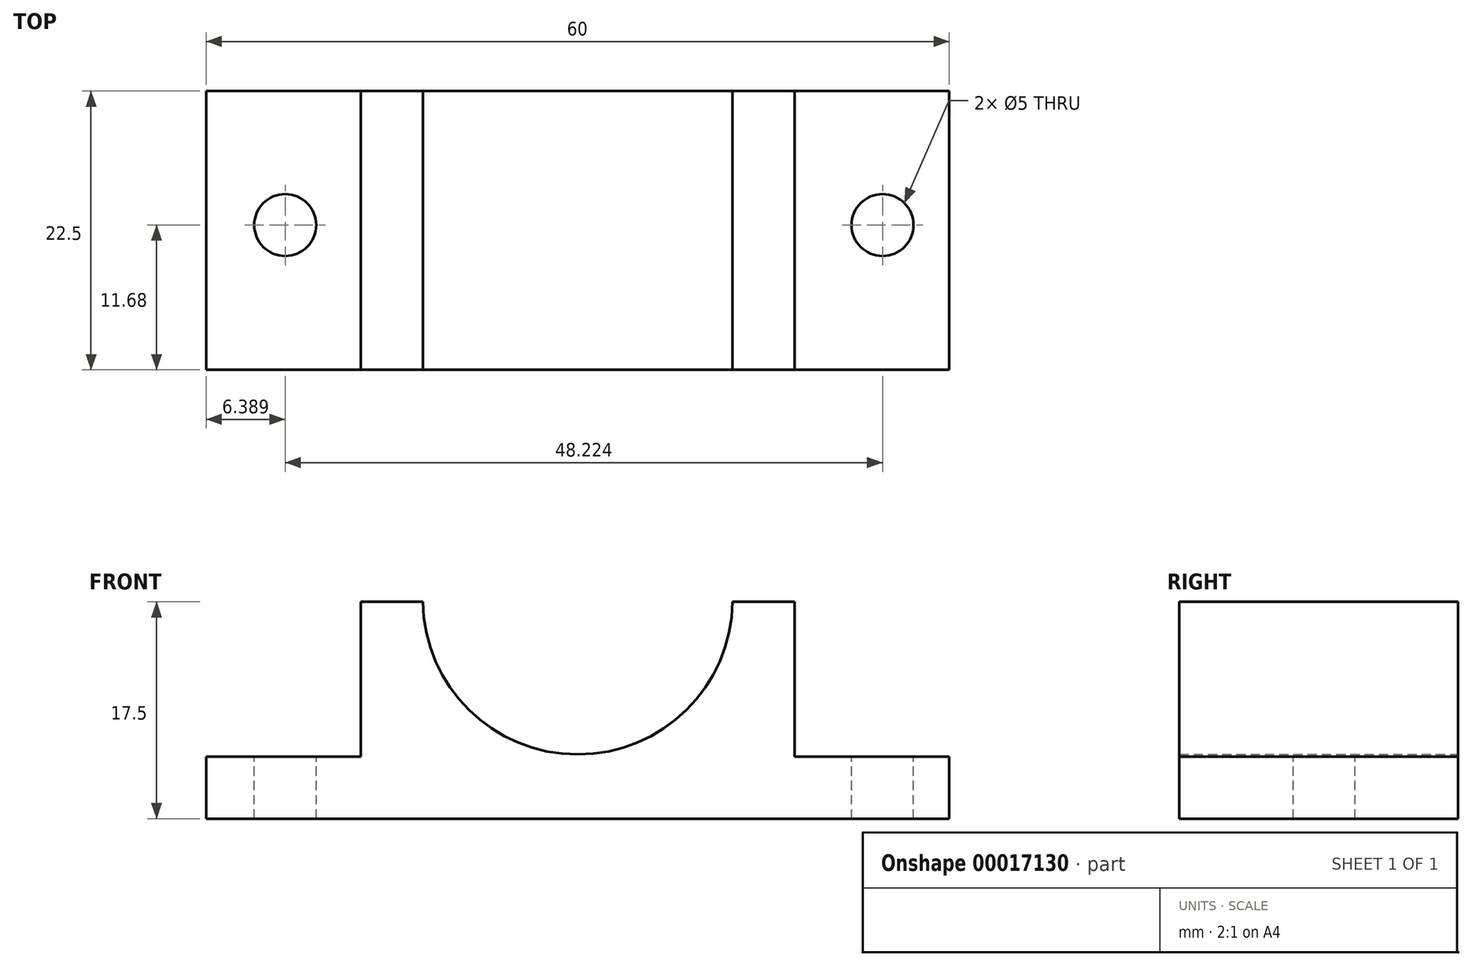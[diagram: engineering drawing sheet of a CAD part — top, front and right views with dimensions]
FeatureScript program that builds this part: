
annotation { "Feature Type Name" : "Feature", "Feature Type Description" : "" }
export const myFeature = defineFeature(function(context is Context, id is Id, definition is map)
    precondition{}
    {
        {
            var Q0;
            Q0=qCreatedBy(makeId("Front.planeOp"),FACE);
            var sketch = newSketch(context, id + "F0", { "sketchPlane" : qUnion([Q0])});
            skLineSegment(sketch, "E0.top", {"start": v(-15.67, -12.96) * mm, "end": v(44.33, -12.96) * mm});
            skLineSegment(sketch, "E0.left", {"start": v(-15.67, -7.96) * mm, "end": v(-15.67, -12.96) * mm});
            skLineSegment(sketch, "E0.right", {"start": v(44.33, -7.96) * mm, "end": v(44.33, -12.96) * mm});
            skLineSegment(sketch, "E1.left", {"start": v(-3.17, -7.96) * mm, "end": v(-3.17, 4.54) * mm});
            skLineSegment(sketch, "E1.right", {"start": v(31.83, -7.96) * mm, "end": v(31.83, 4.54) * mm});
            skArc(sketch, "E2", {"start": v(1.83, 4.54) * mm, "mid": v(14.33, -7.78) * mm, "end": v(26.83, 4.54) * mm});
            skLineSegment(sketch, "E3", {"start": v(-15.67, -7.96) * mm, "end": v(-3.17, -7.96) * mm});
            skLineSegment(sketch, "E4", {"start": v(31.83, -7.96) * mm, "end": v(44.33, -7.96) * mm});
            skLineSegment(sketch, "E5", {"start": v(-3.17, 4.54) * mm, "end": v(1.83, 4.54) * mm});
            skLineSegment(sketch, "E6", {"start": v(26.83, 4.54) * mm, "end": v(31.83, 4.54) * mm});
            skSolve(sketch);
        }
        {
            var Q0;
            Q0=makeQuery(id+"F0.imprint","IMPRINT",FACE,{"disambiguationData":[TD([[makeQuery(id+"F0.imprint","IMPRINT",EDGE,{"derivedFrom":sQuery(id+"F0.wireOp",EDGE,"E0.top")}),1.0]])]});
            extrude(context, id + "F1", {"entities" : qUnion([Q0]), "depth" : 22.5 * mm});
        }
        {
            var Q0;
            Q0=qCreatedBy(makeId("Top.planeOp"),FACE);
            var sketch = newSketch(context, id + "F2", { "sketchPlane" : qUnion([Q0])});
            skCircle(sketch, "E7", {"center": v(-9.28, -10.82) * mm, "radius": 2.5 * mm});
            skCircle(sketch, "E8", {"center": v(38.94, -10.82) * mm, "radius": 2.5 * mm});
            skSolve(sketch);
        }
        {
            var Q0;
            Q0=makeQuery(id+"F2.imprint","IMPRINT",FACE,{"disambiguationData":[TD([[makeQuery(id+"F2.imprint","IMPRINT",EDGE,{"derivedFrom":sQuery(id+"F2.wireOp",EDGE,"E7")}),1.0]])]});
            var Q1;
            Q1=makeQuery(id+"F2.imprint","IMPRINT",FACE,{"disambiguationData":[TD([[makeQuery(id+"F2.imprint","IMPRINT",EDGE,{"derivedFrom":sQuery(id+"F2.wireOp",EDGE,"E8")}),1.0]])]});
            extrude(context, id + "F3", {"entities" : qUnion([Q0, Q1]), "operationType" : NewBodyOperationType.REMOVE, "oppositeDirection" : true, "depth" : 25 * mm});
        }
    });
